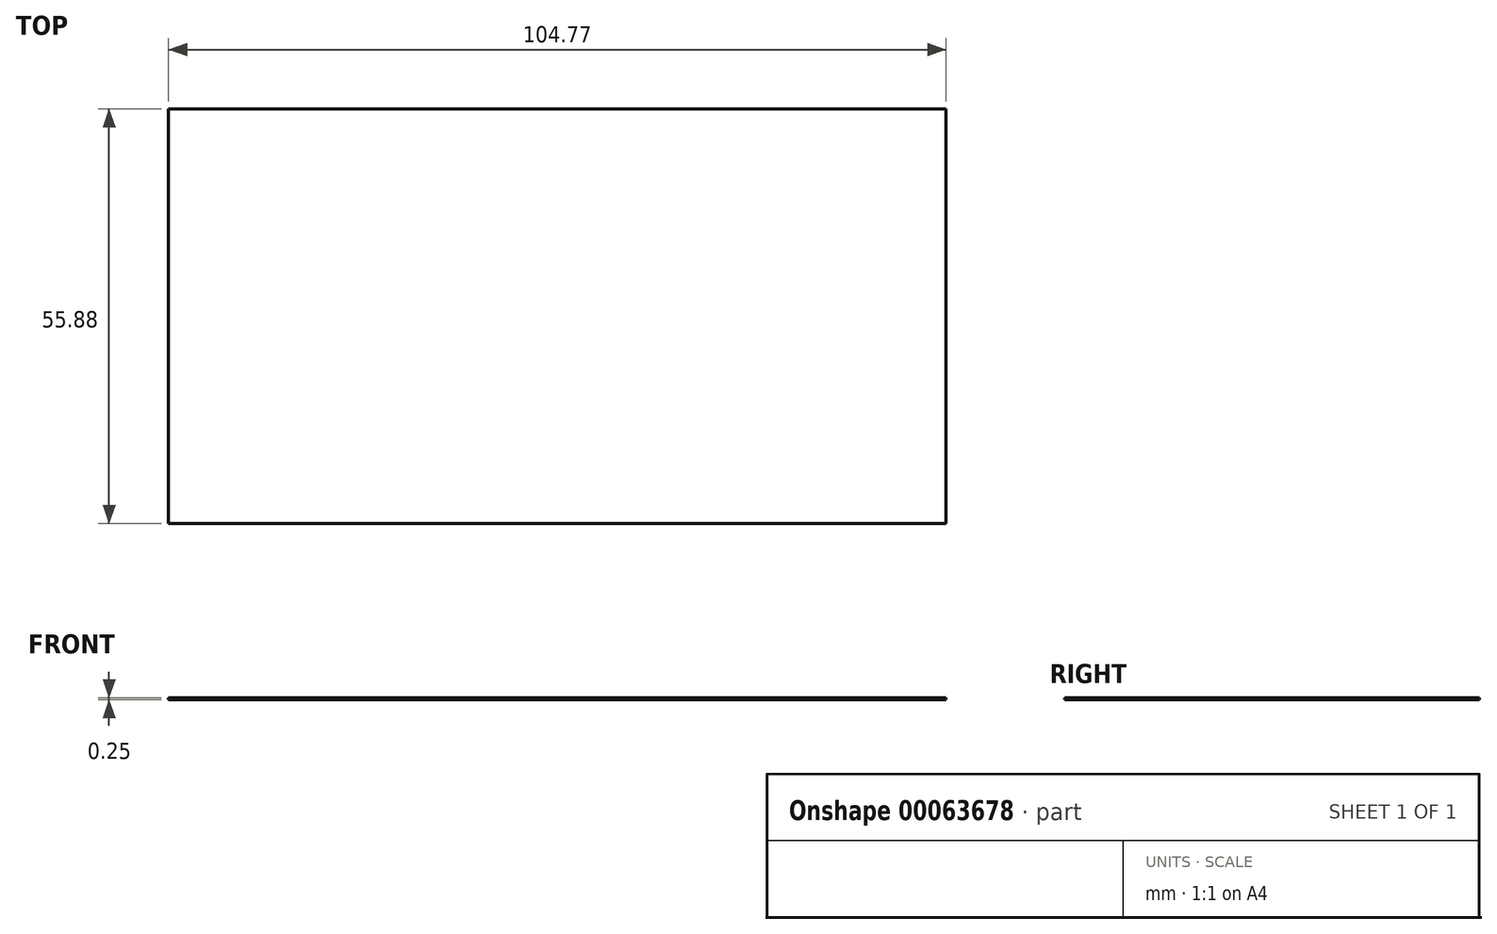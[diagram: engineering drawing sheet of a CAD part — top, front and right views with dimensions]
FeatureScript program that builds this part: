
annotation { "Feature Type Name" : "Feature", "Feature Type Description" : "" }
export const myFeature = defineFeature(function(context is Context, id is Id, definition is map)
    precondition{}
    {
        {
            var Q0;
            Q0=qCreatedBy(makeId("Top.planeOp"),FACE);
            var sketch = newSketch(context, id + "F0", { "sketchPlane" : qUnion([Q0])});
            skLineSegment(sketch, "E0.bottom", {"start": v(-40.18, 0) * mm, "end": v(64.6, 0) * mm});
            skLineSegment(sketch, "E0.top", {"start": v(-40.18, -55.88) * mm, "end": v(64.6, -55.88) * mm});
            skLineSegment(sketch, "E0.left", {"start": v(-40.18, 0) * mm, "end": v(-40.18, -55.88) * mm});
            skLineSegment(sketch, "E0.right", {"start": v(64.6, 0) * mm, "end": v(64.6, -55.88) * mm});
            skSolve(sketch);
        }
        {
            var Q0;
            Q0=makeQuery(id+"F0.imprint","IMPRINT",FACE,{"disambiguationData":[TD([[makeQuery(id+"F0.imprint","IMPRINT",EDGE,{"derivedFrom":sQuery(id+"F0.wireOp",EDGE,"E0.bottom")}),-1.0]])]});
            extrude(context, id + "F1", {"entities" : qUnion([Q0]), "depth" : 0.25 * mm});
        }
    });
